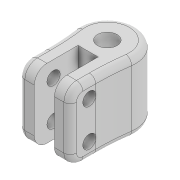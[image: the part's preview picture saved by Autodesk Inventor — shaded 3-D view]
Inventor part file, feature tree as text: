
AUTODESK INVENTOR PART (.ipt)
format: ipt  version: 2022 (Build 260153000, 153)  size: 219,136 bytes
history: native  units: mm
features: extrude x4, sketch x3, fillet x3
ambient origin geometry x8: Origin, YZ Plane, XZ Plane, XY Plane, X Axis, Y Axis, Z Axis, Center Point
bodies: Solid1 (feature_tree)
feature tree (10):
  extrude  "Extrusion1"  Depth=9.0mm
  sketch  "Sketch2"  dims[d2=11.0mm d3=0.0mm d4=3.2mm]
  extrude  "Extrusion2"  Depth=11.0mm
  extrude  "Extrusion4"  Depth=40.0mm
  extrude  "Extrusion3"  Depth=40.0mm
  fillet  "Fillet5"  Radius=10.0mm
  fillet  "Fillet3"  Radius=11.0mm
  fillet  "Fillet4"  Radius=2.1mm
  sketch  "Sketch1"  dims[d0=3.1mm d1=9.0mm]
  sketch  "Sketch3"  dims[d5=1.6mm d6=2.5mm d7=2.5mm d8=10.0mm d9=11.0mm d10=0.0mm d11=2.1mm d12=2.1mm d13=2.0mm d14=2.0mm d15=1.5mm d16=1.5mm d17=11.0mm d18=0.0mm d21=2.0mm d22=1.0mm d23=11.0mm d24=0.0mm d25=1.5mm d26=40.0mm]
